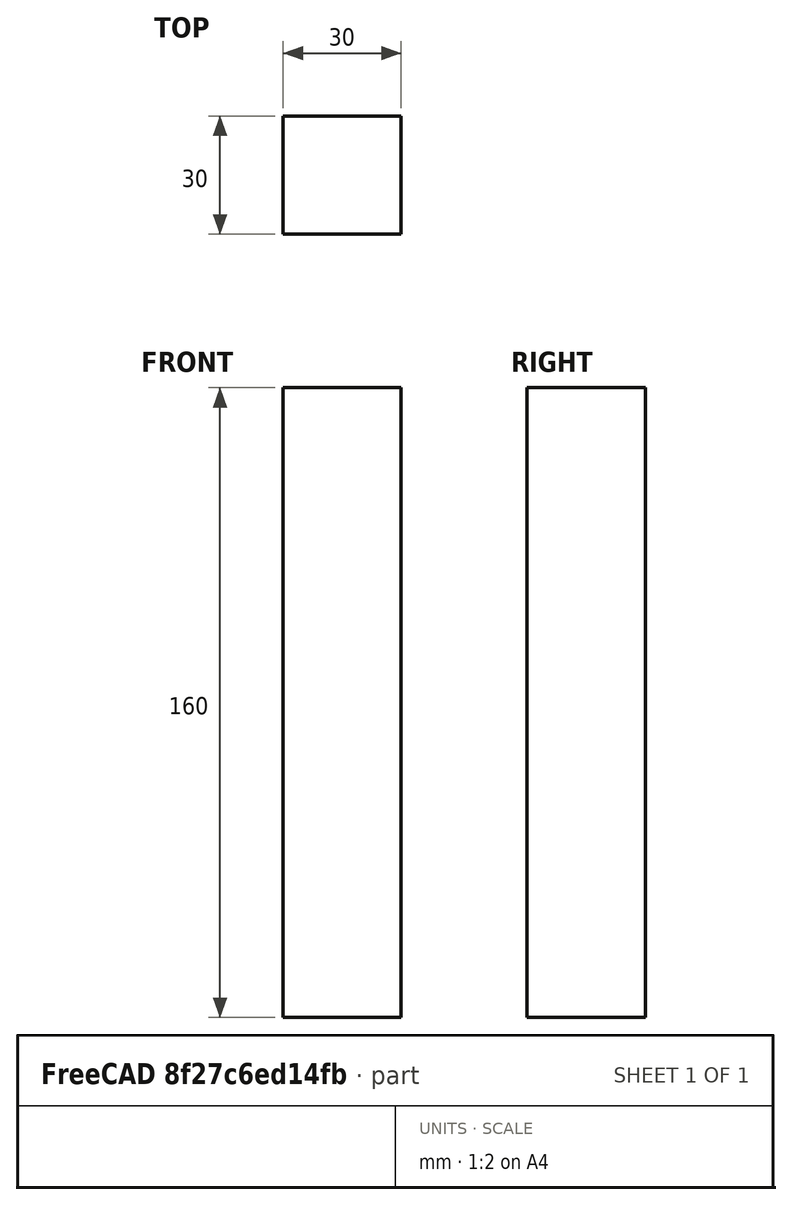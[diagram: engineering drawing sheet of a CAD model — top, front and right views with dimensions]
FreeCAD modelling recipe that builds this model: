
FCSTD DOCUMENT  (FreeCAD 0.20R29177 (Git))
Label: framecorner
License: All rights reserved
LicenseURL: http://en.wikipedia.org/wiki/All_rights_reserved
objects: Sketcher::SketchObject×1, PartDesign::Pad×1, PartDesign::Body×1
note: 4 computed .brp shape members not serialized (recipe doc carries the construction recipe); baked Part::Feature solids carry a one-line shape summary decoded from their .brp

FEATURE [Sketcher::SketchObject] Sketch
  FullyConstrained = true
  MapMode = 5
  Support = -> [XY_Plane]
  sketch-geometry (4):
    g0: LineSegment StartX=0 StartY=0 StartZ=0 EndX=30 EndY=0 EndZ=0
    g1: LineSegment StartX=30 StartY=0 StartZ=0 EndX=30 EndY=30 EndZ=0
    g2: LineSegment StartX=30 StartY=30 StartZ=0 EndX=0 EndY=30 EndZ=0
    g3: LineSegment StartX=0 StartY=30 StartZ=0 EndX=0 EndY=0 EndZ=0
  constraints (11):
    c: Coincident(g0,g1)
    c: Coincident(g1,g2)
    c: Coincident(g2,g3)
    c: Coincident(g3,g0)
    c: Horizontal(g0)
    c: Horizontal(g2)
    c: Vertical(g1)
    c: Vertical(g3)
    c: Coincident(g0,g-1)
    c: Equal(g1,g2)
    c: DistanceY(g1,g1) = 30
FEATURE [PartDesign::Pad] Pad
  Direction = (1,1,1)
  Length = 160
  Length2 = 100
  Profile = -> Sketch
  Type = 0
FEATURE [PartDesign::Body] Body  label="framecorner"
  Group = -> [Sketch,Pad]
  Origin = -> Origin
  Tip = -> Pad
